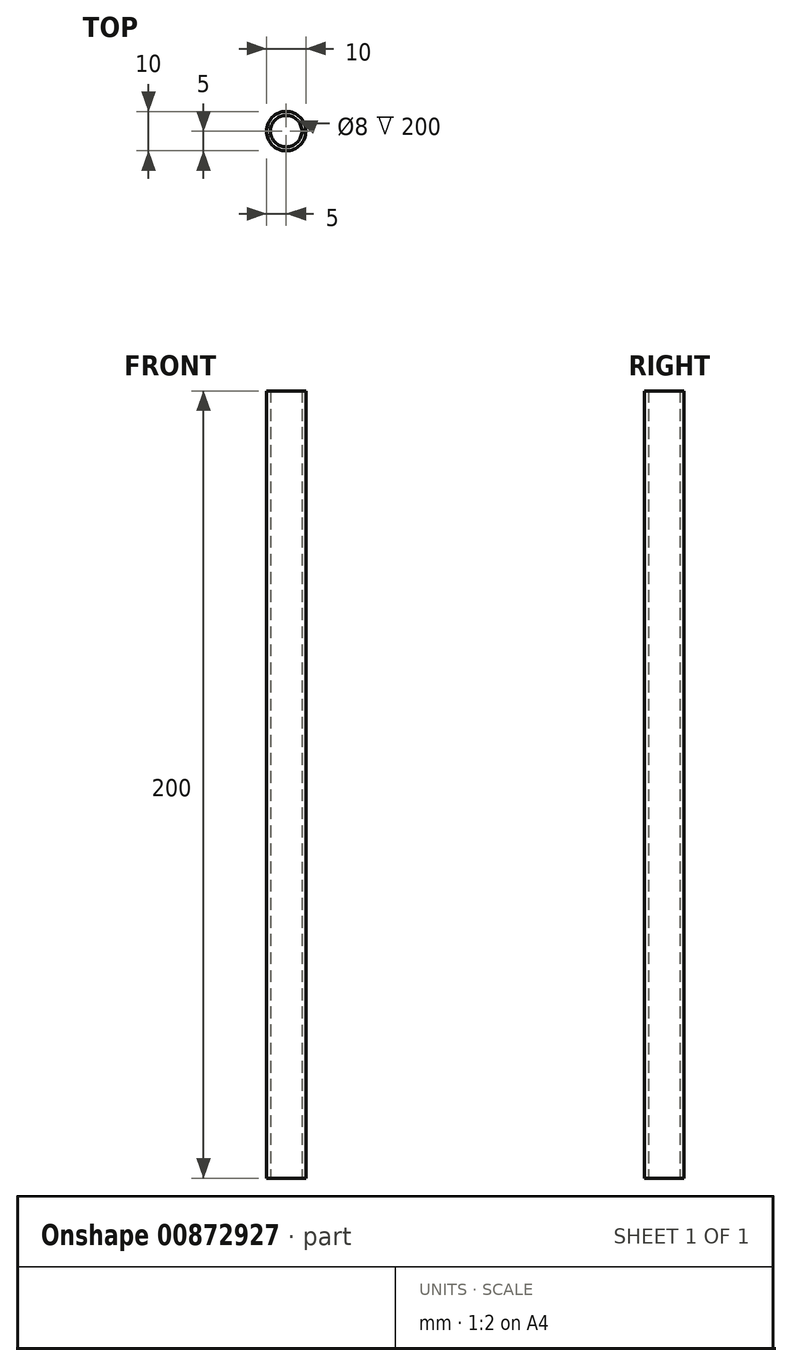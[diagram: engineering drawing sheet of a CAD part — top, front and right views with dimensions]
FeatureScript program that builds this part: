
annotation { "Feature Type Name" : "Feature", "Feature Type Description" : "" }
export const myFeature = defineFeature(function(context is Context, id is Id, definition is map)
    precondition{}
    {
        {
            var Q0;
            Q0=qCreatedBy(makeId("Top.planeOp"),FACE);
            var sketch = newSketch(context, id + "F0", { "sketchPlane" : qUnion([Q0])});
            skCircle(sketch, "E0", {"center": v(0, 0) * mm, "radius": 4 * mm});
            skCircle(sketch, "E1", {"center": v(0, 0) * mm, "radius": 5 * mm});
            skSolve(sketch);
        }
        {
            var Q0;
            Q0=qSketchRegion(id+"F0",true);
            extrude(context, id + "F1", {"entities" : qUnion([Q0]), "endBound" : BoundingType.SYMMETRIC, "depth" : 200 * mm, "offsetDistance" : 25 * mm});
        }
    });
